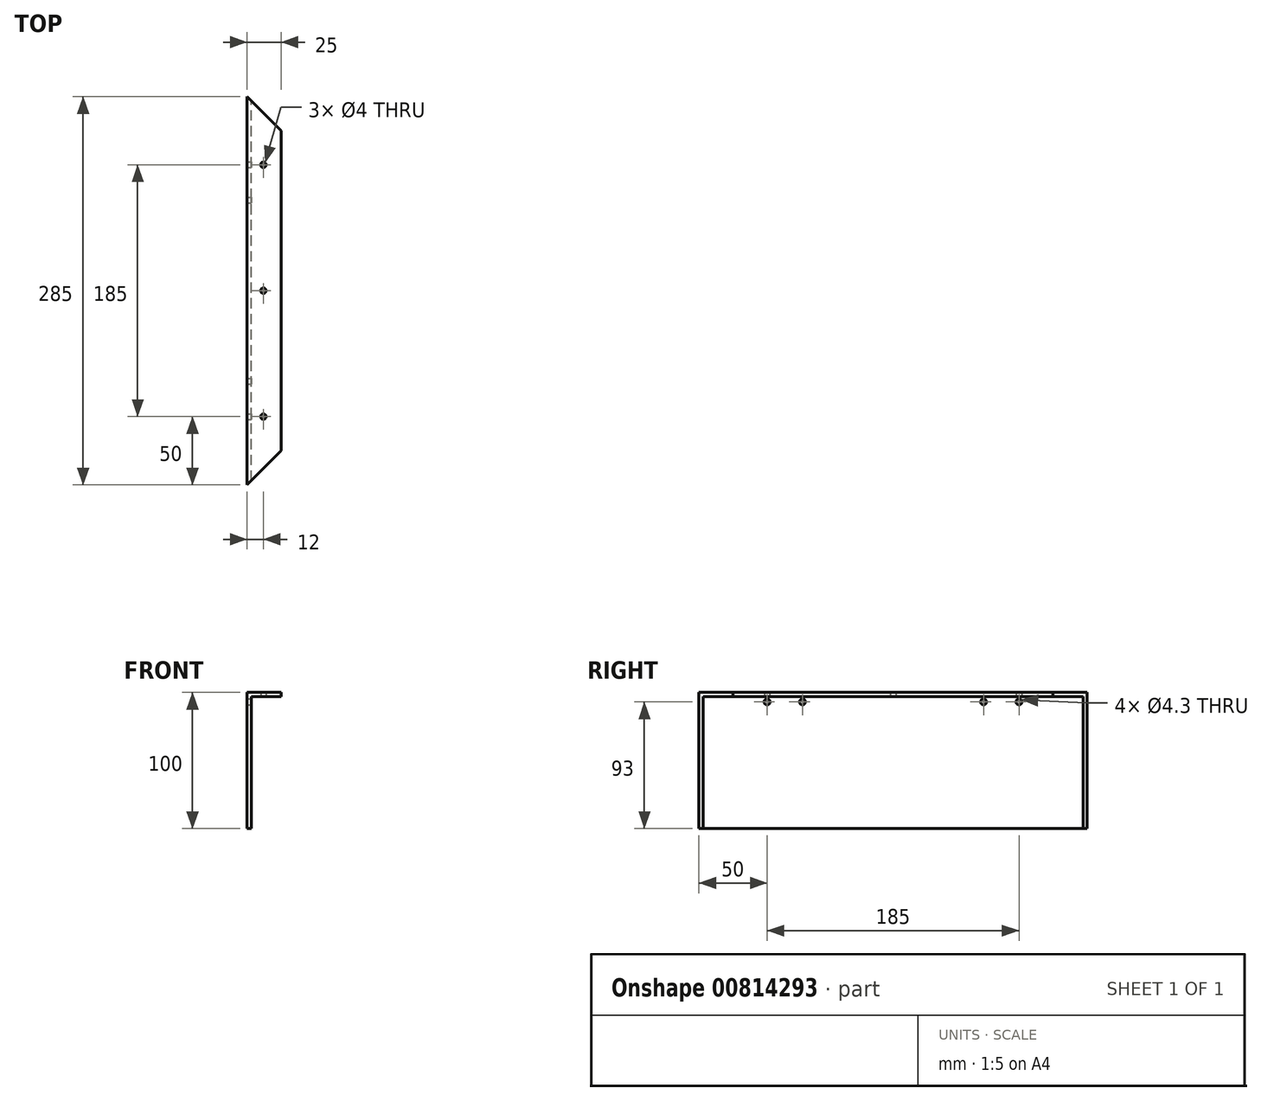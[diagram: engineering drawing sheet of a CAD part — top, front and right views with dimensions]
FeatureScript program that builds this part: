
annotation { "Feature Type Name" : "Feature", "Feature Type Description" : "" }
export const myFeature = defineFeature(function(context is Context, id is Id, definition is map)
    precondition{}
    {
        {
            var Q0;
            Q0=qCreatedBy(makeId("Front.planeOp"),FACE);
            var sketch = newSketch(context, id + "F0", { "sketchPlane" : qUnion([Q0])});
            skLineSegment(sketch, "E0.bottom", {"start": v(1.5, 50) * mm, "end": v(-1.5, 50) * mm});
            skLineSegment(sketch, "E0.top", {"start": v(1.5, -50) * mm, "end": v(-1.5, -50) * mm});
            skLineSegment(sketch, "E0.left", {"start": v(1.5, 50) * mm, "end": v(1.5, -50) * mm});
            skLineSegment(sketch, "E0.right", {"start": v(-1.5, 50) * mm, "end": v(-1.5, -50) * mm});
            skPoint(sketch, "E0.middle", {"position": v(0, 0) * mm});
            skLineSegment(sketch, "E1.bottom", {"start": v(1.5, 50) * mm, "end": v(23.5, 50) * mm});
            skLineSegment(sketch, "E1.top", {"start": v(1.5, 47) * mm, "end": v(23.5, 47) * mm});
            skLineSegment(sketch, "E1.left", {"start": v(1.5, 50) * mm, "end": v(1.5, 47) * mm});
            skLineSegment(sketch, "E1.right", {"start": v(23.5, 50) * mm, "end": v(23.5, 47) * mm});
            skSolve(sketch);
        }
        {
            var Q0;
            Q0=makeQuery(id+"F0.imprint","IMPRINT",FACE,{"disambiguationData":[TD([[makeQuery(id+"F0.imprint","IMPRINT",EDGE,{"derivedFrom":sQuery(id+"F0.wireOp",EDGE,"E1.bottom")}),-1.0]])]});
            var Q1;
            Q1=makeQuery(id+"F0.imprint","IMPRINT",FACE,{"disambiguationData":[TD([[makeQuery(id+"F0.imprint","IMPRINT",EDGE,{"derivedFrom":sQuery(id+"F0.wireOp",EDGE,"E0.bottom")}),1.0]])]});
            extrude(context, id + "F1", {"entities" : qUnion([Q0, Q1]), "depth" : 285 * mm, "offsetDistance" : 25 * mm, "symmetric" : true});
        }
        {
            var Q0;
            Q0=makeQuery(id+"F1.opExtrude","SWEPT_FACE",FACE,{"disambiguationData":[OSD([sQuery(id+"F0.wireOp",EDGE,"E0.right")])]});
            var sketch = newSketch(context, id + "F2", { "sketchPlane" : qUnion([Q0])});
            skPoint(sketch, "E2", {"position": v(-92.5, 43) * mm});
            skPoint(sketch, "E3", {"position": v(-66.5, 43) * mm});
            skPoint(sketch, "E4", {"position": v(66.5, 43) * mm});
            skPoint(sketch, "E5", {"position": v(92.5, 43) * mm});
            skSolve(sketch);
        }
        {
            var Q0;
            Q0=sQuery(id+"F2.wireOp",VERTEX,"E2");
            var Q1;
            Q1=sQuery(id+"F2.wireOp",VERTEX,"E3");
            var Q2;
            Q2=sQuery(id+"F2.wireOp",VERTEX,"E4");
            var Q3;
            Q3=sQuery(id+"F2.wireOp",VERTEX,"E5");
            var Q4;
            Q4=makeQuery(id+"F1.opExtrude","SWEPT_BODY",BODY,{"disambiguationData":[OSD([sQuery(id+"F0.wireOp",EDGE,"E0.bottom"),sQuery(id+"F0.wireOp",EDGE,"E0.top"),sQuery(id+"F0.wireOp",EDGE,"E0.left"),sQuery(id+"F0.wireOp",EDGE,"E0.right"),sQuery(id+"F0.wireOp",EDGE,"E1.bottom"),sQuery(id+"F0.wireOp",EDGE,"E1.top"),sQuery(id+"F0.wireOp",EDGE,"E1.right")])]});
            hole(context, id + "F3", {"style" : HoleStyle.SIMPLE, "endStyle" : HoleEndStyle.BLIND, "holeDiameter" : 4.3 * mm, "majorDiameter" : 5 * mm, "holeDepth" : 3 * mm, "isTappedThrough" : true, "tappedDepth" : 12 * mm, "tapClearance" : 3, "locations" : qUnion([Q0, Q1, Q2, Q3]), "scope" : qUnion([Q4]), "startStyle" : HoleStartStyle.SKETCH});
        }
        {
            var Q0;
            Q0=makeQuery(id+"F1.opExtrude","SWEPT_FACE",FACE,{"disambiguationData":[OSD([sQuery(id+"F0.wireOp",EDGE,"E0.bottom"),sQuery(id+"F0.wireOp",EDGE,"E1.bottom")])]});
            var sketch = newSketch(context, id + "F4", { "sketchPlane" : qUnion([Q0])});
            skPoint(sketch, "E6", {"position": v(10.5, -92.5) * mm});
            skPoint(sketch, "E7", {"position": v(10.5, 0) * mm});
            skPoint(sketch, "E8", {"position": v(10.5, 92.5) * mm});
            skSolve(sketch);
        }
        {
            var Q0;
            Q0=sQuery(id+"F4.wireOp",VERTEX,"E8");
            var Q1;
            Q1=sQuery(id+"F4.wireOp",VERTEX,"E7");
            var Q2;
            Q2=sQuery(id+"F4.wireOp",VERTEX,"E6");
            var Q3;
            Q3=makeQuery(id+"F1.opExtrude","SWEPT_BODY",BODY,{"disambiguationData":[OSD([sQuery(id+"F0.wireOp",EDGE,"E0.bottom"),sQuery(id+"F0.wireOp",EDGE,"E0.top"),sQuery(id+"F0.wireOp",EDGE,"E0.left"),sQuery(id+"F0.wireOp",EDGE,"E0.right"),sQuery(id+"F0.wireOp",EDGE,"E1.bottom"),sQuery(id+"F0.wireOp",EDGE,"E1.top"),sQuery(id+"F0.wireOp",EDGE,"E1.right")])]});
            hole(context, id + "F5", {"style" : HoleStyle.SIMPLE, "endStyle" : HoleEndStyle.BLIND, "holeDiameter" : 4 * mm, "majorDiameter" : 5 * mm, "holeDepth" : 3 * mm, "isTappedThrough" : true, "tappedDepth" : 12 * mm, "tapClearance" : 3, "locations" : qUnion([Q0, Q1, Q2]), "scope" : qUnion([Q3]), "startStyle" : HoleStartStyle.SKETCH});
        }
        {
            var Q0;
            Q0=makeQuery(id+"F1.opExtrude","SWEPT_FACE",FACE,{"disambiguationData":[OSD([sQuery(id+"F0.wireOp",EDGE,"E0.bottom"),sQuery(id+"F0.wireOp",EDGE,"E1.bottom")])]});
            var sketch = newSketch(context, id + "F6", { "sketchPlane" : qUnion([Q0])});
            skLineSegment(sketch, "E9", {"start": v(-1.5, 142.5) * mm, "end": v(23.5, 142.5) * mm});
            skLineSegment(sketch, "E10", {"start": v(23.5, 142.5) * mm, "end": v(23.5, 117.5) * mm});
            skLineSegment(sketch, "E11", {"start": v(23.5, 117.5) * mm, "end": v(-1.5, 142.5) * mm});
            skLineSegment(sketch, "E12", {"start": v(-1.5, -142.5) * mm, "end": v(23.5, -142.5) * mm});
            skLineSegment(sketch, "E13", {"start": v(23.5, -142.5) * mm, "end": v(23.5, -117.5) * mm});
            skLineSegment(sketch, "E14", {"start": v(23.5, -117.5) * mm, "end": v(-1.5, -142.5) * mm});
            skSolve(sketch);
        }
        {
            var Q0;
            Q0 = qSketchRegion(id + "F6", true);
            extrude(context, id + "F7", {"entities" : qUnion([Q0]), "operationType" : NewBodyOperationType.REMOVE, "oppositeDirection" : true, "depth" : 100 * mm, "offsetDistance" : 25 * mm});
        }
    });
